# Revit family: Door_Swing Door_The Sliding Door Company_Single Door with Transom_Without Casing
name_source: partatom
category: Doors
units: mm (PartAtom-declared; Revit-internal decimal feet)

## family parameters
Always vertical = Yes
Cut with Voids When Loaded = No
Host = Wall
OmniClass Number = 23.30.10.00
OmniClass Title = Doors
Room Calculation Point = No
Shared = No

## types (1)
- Single Swing Door with Transom
    ADA Opening Clearance = Minimum of 32 inches Opening Clearance
    Beam = 2"
    Description = Swing Door without Door Casing + Transom
    Finished Opening Height = 120"
    Frame Projection Ext. = 1"
    Frame Projection Int. = 1"
    Frame Width = 3"
    Function = Interior
    Height = 96"
    Kickplate = Yes
    Lever Set = Yes
    Manufacturer = The Sliding Door Company
    Maximum Door Panel Height = 108 inches
    Maximum Door Panel Width = 40 inches
    Maximum Door Swing = 120 degress
    Maximum Transom Order Height = 48 inches
    Model = Swing Door without Door Casing + Transom
    Opening Clearance Height = 95 1/2"
    Opening Clearance Width = 37 1/2"
    Round Designer Handle 12" = No
    SD Bottom Side Gap = 5/8"
    SD Handle Side Gap = 1/8"
    SD Hinge Side Gap = 1/4"
    SD Order Height = 96"
    SD Order Width = 40"
    SD Panel Height = 95 1/8"
    SD Panel Width = 39 5/8"
    SD Stile/Rail = 3"
    SD Top Side Gap = 1/4"
    Thickness = 1 1/4"
    Transom Order Height = 22"
    Transom Order Width = 40"
    Transom Panel Height = 20 1/2"
    Transom Panel Width = 38"
    URL = https://www.slidingdoorco.com
    Wall Closure = By host
    Width = 40"

## geometry (parser evidence)
native form markers: Sweep x9
no freeform markers — native parametric forms only
